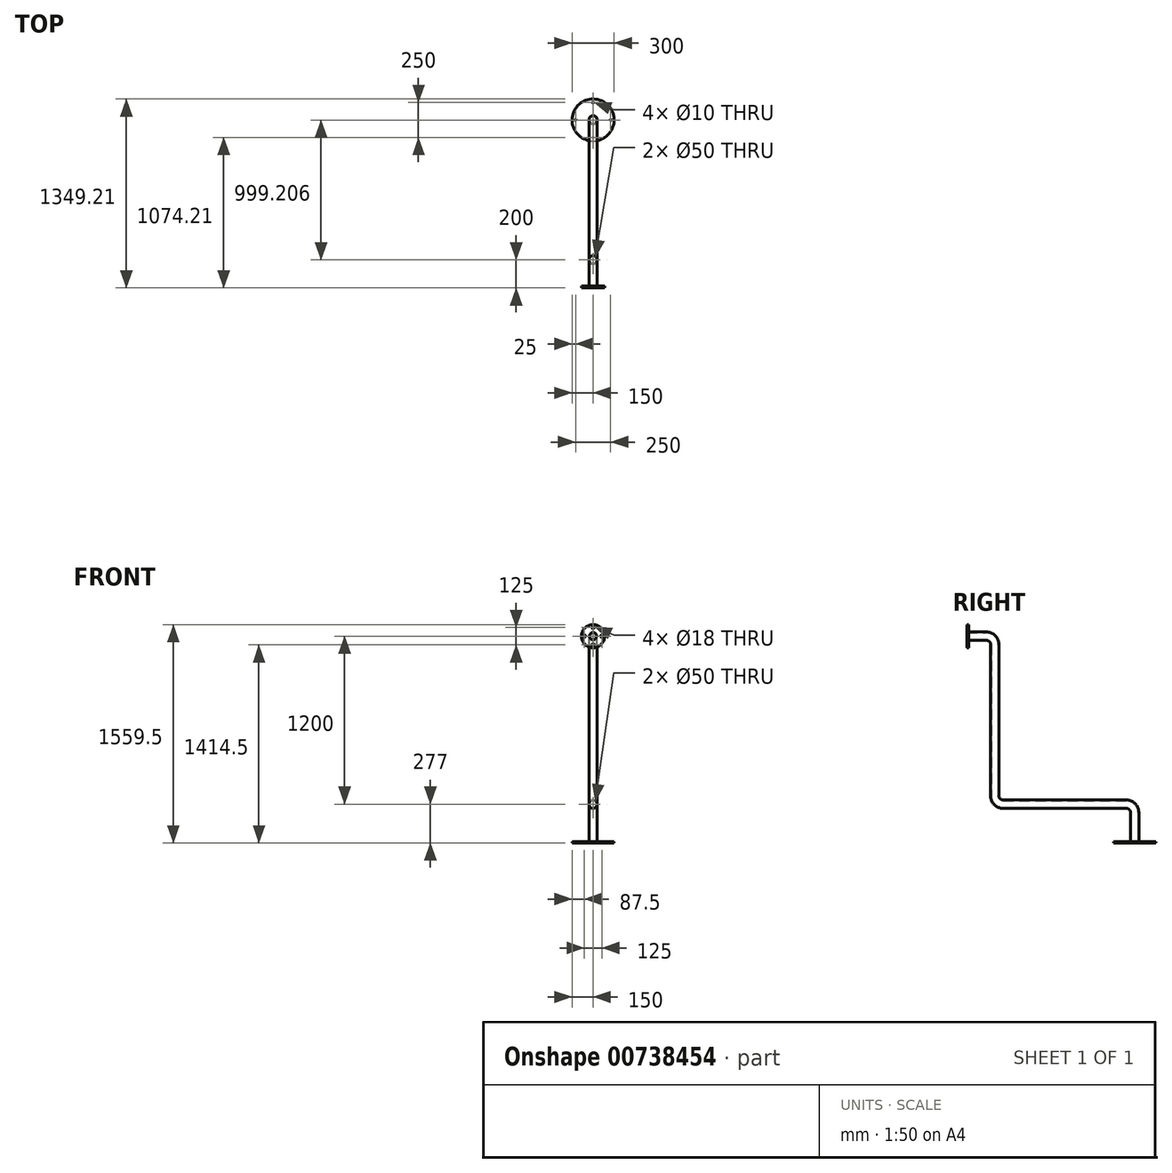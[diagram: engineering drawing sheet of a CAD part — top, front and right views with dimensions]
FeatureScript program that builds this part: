
annotation { "Feature Type Name" : "Feature", "Feature Type Description" : "" }
export const myFeature = defineFeature(function(context is Context, id is Id, definition is map)
    precondition{}
    {
        {
            var Q0;
            Q0=qCreatedBy(makeId("Front.planeOp"),FACE);
            var sketch = newSketch(context, id + "F0", { "sketchPlane" : qUnion([Q0])});
            skCircle(sketch, "E0", {"center": v(0, 0) * mm, "radius": 25 * mm});
            skCircle(sketch, "E1", {"center": v(0, 0) * mm, "radius": 82.5 * mm});
            skCircle(sketch, "E2", {"center": v(0, 62.5) * mm, "radius": 9 * mm});
            skCircle(sketch, "E3.1.0", {"center": v(-62.5, 0) * mm, "radius": 9 * mm});
            skCircle(sketch, "E3.2.0", {"center": v(0, -62.5) * mm, "radius": 9 * mm});
            skCircle(sketch, "E3.3.0", {"center": v(62.5, 0) * mm, "radius": 9 * mm});
            skCircle(sketch, "E4", {"center": v(0, 0) * mm, "radius": 30 * mm});
            skSolve(sketch);
        }
        {
            var Q0;
            Q0=qCreatedBy(makeId("Right.planeOp"),FACE);
            var sketch = newSketch(context, id + "F1", { "sketchPlane" : qUnion([Q0])});
            skLineSegment(sketch, "E5", {"start": v(0, 0) * mm, "end": v(140, 0) * mm});
            skLineSegment(sketch, "E6", {"start": v(200, -60) * mm, "end": v(200, -1140) * mm});
            skPoint(sketch, "E7.visualSharp", {"position": v(200, 0) * mm});
            skArc(sketch, "E7.filletArc", {"start": v(200, -60) * mm, "mid": v(182.43, -17.57) * mm, "end": v(140, 0) * mm});
            skLineSegment(sketch, "E8", {"start": v(260, -1200) * mm, "end": v(1139.2, -1200) * mm});
            skLineSegment(sketch, "E9", {"start": v(1199.2, -1260) * mm, "end": v(1199.2, -1477) * mm});
            skPoint(sketch, "E10.visualSharp", {"position": v(200, -1200) * mm});
            skArc(sketch, "E10.filletArc", {"start": v(200, -1140) * mm, "mid": v(217.57, -1182.43) * mm, "end": v(260, -1200) * mm});
            skPoint(sketch, "E11.visualSharp", {"position": v(1199.2, -1200) * mm});
            skArc(sketch, "E11.filletArc", {"start": v(1199.2, -1260) * mm, "mid": v(1181.63, -1217.57) * mm, "end": v(1139.2, -1200) * mm});
            skSolve(sketch);
        }
        {
            var Q0;
            Q0=makeQuery(id+"F0.imprint","IMPRINT",FACE,{"disambiguationData":[TD([[makeQuery(id+"F0.imprint","IMPRINT",EDGE,{"derivedFrom":sQuery(id+"F0.wireOp",EDGE,"E0")}),-1.0]])]});
            var Q1;
            Q1=sQuery(id+"F1.wireOp",EDGE,"E5");
            var Q2;
            Q2=sQuery(id+"F1.wireOp",EDGE,"E7.filletArc");
            var Q3;
            Q3=sQuery(id+"F1.wireOp",EDGE,"E6");
            var Q4;
            Q4=sQuery(id+"F1.wireOp",EDGE,"E10.filletArc");
            var Q5;
            Q5=sQuery(id+"F1.wireOp",EDGE,"E8");
            var Q6;
            Q6=sQuery(id+"F1.wireOp",EDGE,"E11.filletArc");
            var Q7;
            Q7=sQuery(id+"F1.wireOp",EDGE,"E9");
            sweep(context, id + "F2", {"profiles" : qUnion([Q0]), "path" : qUnion([Q1, Q2, Q3, Q4, Q5, Q6, Q7])});
        }
        {
            var Q0;
            Q0=makeQuery(id+"F0.imprint","IMPRINT",FACE,{"disambiguationData":[TD([[makeQuery(id+"F0.imprint","IMPRINT",EDGE,{"derivedFrom":sQuery(id+"F0.wireOp",EDGE,"E1")}),1.0]])]});
            extrude(context, id + "F3", {"entities" : qUnion([Q0]), "operationType" : NewBodyOperationType.ADD, "oppositeDirection" : true, "depth" : 15 * mm, "offsetDistance" : 25 * mm});
        }
        {
            var Q0;
            Q0=makeQuery(id+"F2.opSweep","CAP_FACE",FACE,{"disambiguationData":[OSD([sQuery(id+"F0.wireOp",EDGE,"E0"),sQuery(id+"F0.wireOp",EDGE,"E4"),sQuery(id+"F1.wireOp",VERTEX,"E9.end")])],"isStart":false});
            var sketch = newSketch(context, id + "F4", { "sketchPlane" : qUnion([Q0])});
            skCircle(sketch, "E12", {"center": v(0, -1199.2) * mm, "radius": 150 * mm});
            skCircle(sketch, "E13", {"center": v(0, -1324.2) * mm, "radius": 5 * mm});
            skCircle(sketch, "E14.1.0", {"center": v(125, -1199.2) * mm, "radius": 5 * mm});
            skCircle(sketch, "E14.2.0", {"center": v(0, -1074.2) * mm, "radius": 5 * mm});
            skCircle(sketch, "E14.3.0", {"center": v(-125, -1199.2) * mm, "radius": 5 * mm});
            skSolve(sketch);
        }
        {
            var Q0;
            Q0=makeQuery(id+"F4.imprint","IMPRINT",FACE,{"disambiguationData":[TD([[makeQuery(id+"F4.imprint","IMPRINT",EDGE,{"derivedFrom":sQuery(id+"F4.wireOp",EDGE,"E12")}),1.0]])]});
            extrude(context, id + "F5", {"entities" : qUnion([Q0]), "operationType" : NewBodyOperationType.ADD, "oppositeDirection" : true, "depth" : 10 * mm, "offsetDistance" : 25 * mm});
        }
    });
